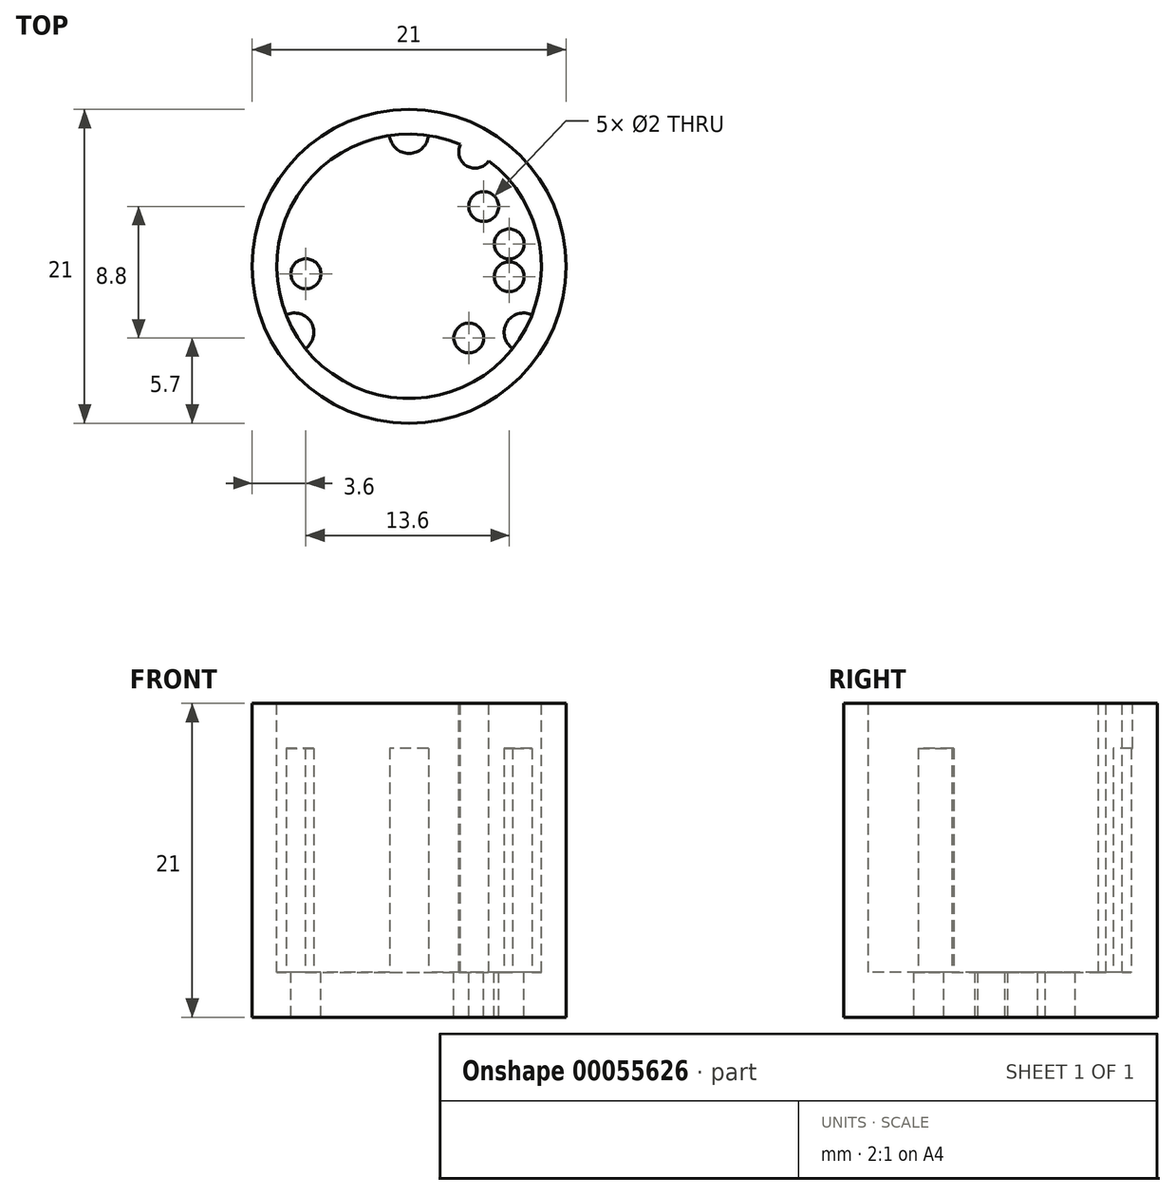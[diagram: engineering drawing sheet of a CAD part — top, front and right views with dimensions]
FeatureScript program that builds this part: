
annotation { "Feature Type Name" : "Feature", "Feature Type Description" : "" }
export const myFeature = defineFeature(function(context is Context, id is Id, definition is map)
    precondition{}
    {
        {
            var Q0;
            Q0=qCreatedBy(makeId("Top.planeOp"),FACE);
            var sketch = newSketch(context, id + "F0", { "sketchPlane" : qUnion([Q0])});
            skCircle(sketch, "E0", {"center": v(0, 0) * mm, "radius": 10.5 * mm});
            skSolve(sketch);
        }
        {
            var Q0;
            Q0 = qSketchRegion(id + "F0", true);
            extrude(context, id + "F1", {"entities" : qUnion([Q0]), "depth" : 21 * mm});
        }
        {
            var Q0;
            Q0=makeQuery(id+"F1.opExtrude","CAP_FACE",FACE,{"disambiguationData":[OSD([sQuery(id+"F0.wireOp",EDGE,"E0")])],"isStart":false});
            var sketch = newSketch(context, id + "F2", { "sketchPlane" : qUnion([Q0])});
            skArc(sketch, "E1", {"start": v(3.44, 8.15) * mm, "mid": v(-4.43, -7.66) * mm, "end": v(5.34, 7.06) * mm});
            skArc(sketch, "E2", {"start": v(3.44, 8.15) * mm, "mid": v(3.88, 6.71) * mm, "end": v(5.34, 7.06) * mm});
            skLineSegment(sketch, "E3", {"start": v(0, 0) * mm, "end": v(4.43, 7.66) * mm});
            skLineSegment(sketch, "E4", {"start": v(0, 0) * mm, "end": v(0, 8.85) * mm});
            skSolve(sketch);
        }
        {
            var Q0;
            Q0 = qSketchRegion(id + "F2", true);
            extrude(context, id + "F3", {"entities" : qUnion([Q0]), "operationType" : NewBodyOperationType.REMOVE, "oppositeDirection" : true, "depth" : 18 * mm});
        }
        {
            var Q0;
            Q0=makeQuery(id+"F3.boolean.opBoolean","COPY",FACE,{"derivedFrom":makeQuery(id+"F3.opExtrude","CAP_FACE",FACE,{"disambiguationData":[OSD([sQuery(id+"F2.wireOp",EDGE,"E1"),sQuery(id+"F2.wireOp",EDGE,"E2")])],"isStart":false})});
            var sketch = newSketch(context, id + "F4", { "sketchPlane" : qUnion([Q0])});
            skCircle(sketch, "E5", {"center": v(-6.9, -0.5) * mm, "radius": 1 * mm});
            skCircle(sketch, "E6", {"center": v(5, 4) * mm, "radius": 1 * mm});
            skCircle(sketch, "E7", {"center": v(6.7, 1.5) * mm, "radius": 1 * mm});
            skCircle(sketch, "E8", {"center": v(4, -4.8) * mm, "radius": 1 * mm});
            skCircle(sketch, "E9", {"center": v(6.7, -0.7) * mm, "radius": 1 * mm});
            skSolve(sketch);
        }
        {
            var Q0;
            Q0 = qSketchRegion(id + "F4", true);
            extrude(context, id + "F5", {"entities" : qUnion([Q0]), "operationType" : NewBodyOperationType.REMOVE, "oppositeDirection" : true, "depth" : 25 * mm});
        }
        {
            var Q0;
            Q0=makeQuery(id+"F3.boolean.opBoolean","COPY",FACE,{"derivedFrom":makeQuery(id+"F3.opExtrude","CAP_FACE",FACE,{"disambiguationData":[OSD([sQuery(id+"F2.wireOp",EDGE,"E1"),sQuery(id+"F2.wireOp",EDGE,"E2")])],"isStart":false})});
            var sketch = newSketch(context, id + "F6", { "sketchPlane" : qUnion([Q0])});
            skCircle(sketch, "E10", {"center": v(0, 8.85) * mm, "radius": 1.3 * mm});
            skLineSegment(sketch, "E11", {"start": v(0, 8.85) * mm, "end": v(0, 0) * mm});
            skLineSegment(sketch, "E12", {"start": v(0, 0) * mm, "end": v(-7.66, -4.42) * mm});
            skLineSegment(sketch, "E13", {"start": v(0, 0) * mm, "end": v(7.66, -4.42) * mm});
            skCircle(sketch, "E14", {"center": v(-7.66, -4.42) * mm, "radius": 1.3 * mm});
            skCircle(sketch, "E15", {"center": v(7.66, -4.42) * mm, "radius": 1.3 * mm});
            skSolve(sketch);
        }
        {
            var Q0;
            Q0 = qSketchRegion(id + "F6", true);
            extrude(context, id + "F7", {"entities" : qUnion([Q0]), "operationType" : NewBodyOperationType.ADD, "depth" : 15 * mm});
        }
    });
